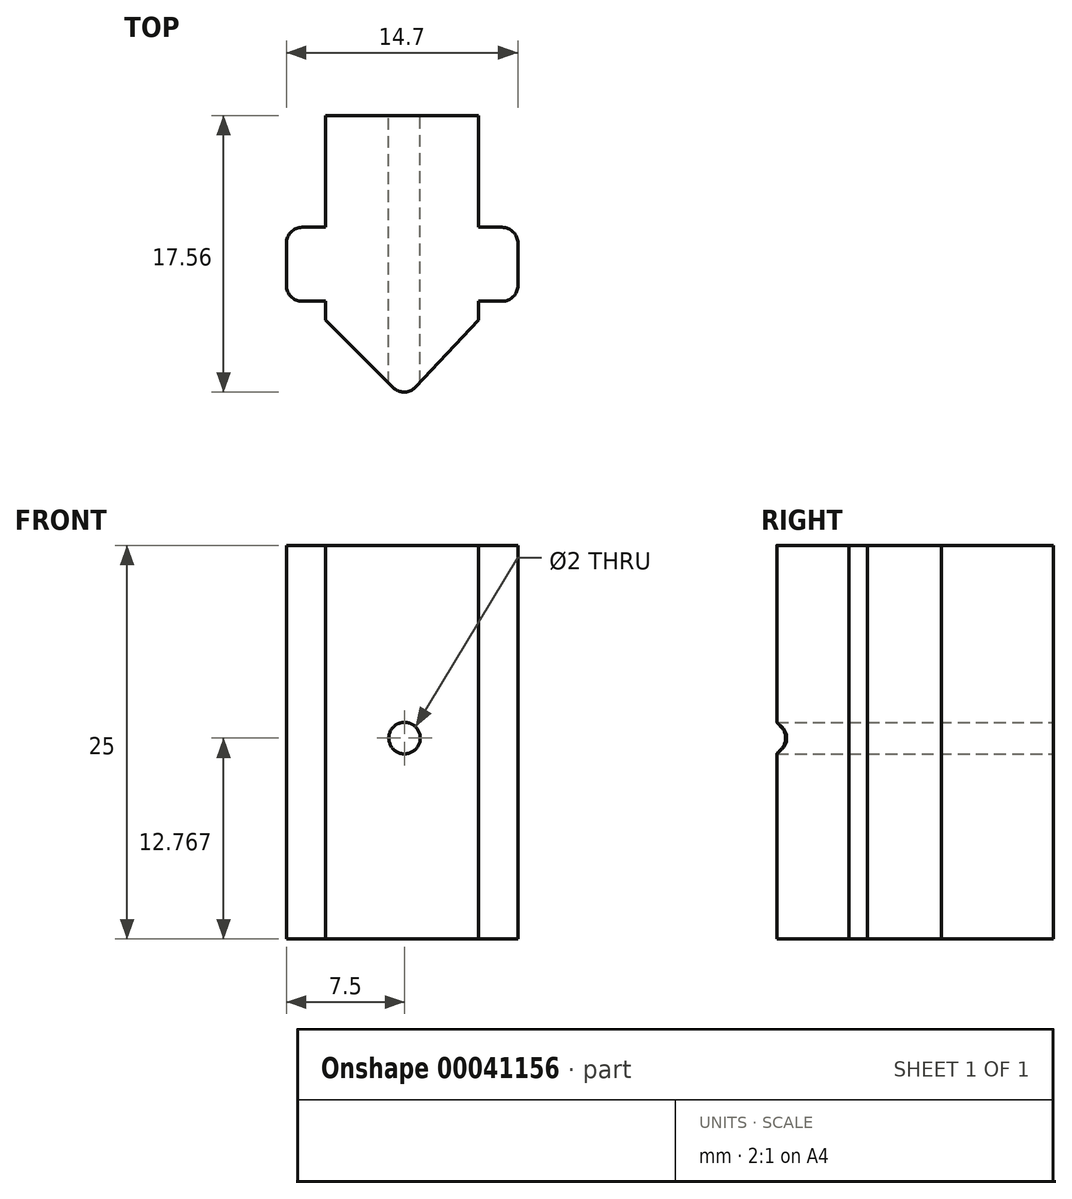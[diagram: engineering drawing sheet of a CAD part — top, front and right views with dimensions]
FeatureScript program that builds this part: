
annotation { "Feature Type Name" : "Feature", "Feature Type Description" : "" }
export const myFeature = defineFeature(function(context is Context, id is Id, definition is map)
    precondition{}
    {
        {
            var Q0;
            Q0=qCreatedBy(makeId("Top.planeOp"),FACE);
            var sketch = newSketch(context, id + "F0", { "sketchPlane" : qUnion([Q0])});
            skLineSegment(sketch, "E0.bottom", {"start": v(-5, 3.37) * mm, "end": v(4.7, 3.37) * mm});
            skLineSegment(sketch, "E0.top", {"start": v(-5, -9.63) * mm, "end": v(4.7, -9.63) * mm});
            skLineSegment(sketch, "E0.left", {"start": v(-5, 3.37) * mm, "end": v(-5, -9.63) * mm});
            skLineSegment(sketch, "E0.right", {"start": v(4.7, 3.37) * mm, "end": v(4.7, -9.63) * mm});
            skLineSegment(sketch, "E1.bottom", {"start": v(7.2, -3.73) * mm, "end": v(-7.5, -3.73) * mm});
            skLineSegment(sketch, "E1.top", {"start": v(7.2, -8.43) * mm, "end": v(-7.5, -8.43) * mm});
            skLineSegment(sketch, "E1.left", {"start": v(7.2, -3.73) * mm, "end": v(7.2, -8.43) * mm});
            skLineSegment(sketch, "E1.right", {"start": v(-7.5, -3.73) * mm, "end": v(-7.5, -8.43) * mm});
            skLineSegment(sketch, "E2", {"start": v(-5, -9.63) * mm, "end": v(0, -14.63) * mm});
            skLineSegment(sketch, "E3", {"start": v(0, -14.63) * mm, "end": v(4.7, -9.63) * mm});
            skSolve(sketch);
        }
        {
            var Q0;
            Q0=qSketchRegion(id+"F0",true);
            extrude(context, id + "F1", {"entities" : qUnion([Q0]), "depth" : 25 * mm});
        }
        {
            var Q0;
            Q0=makeQuery(id+"F1.opExtrude","SWEPT_EDGE",EDGE,{"disambiguationData":[OSD([sQuery(id+"F0.wireOp",EDGE,"E1.bottom"),sQuery(id+"F0.wireOp",EDGE,"E1.right")])]});
            var Q1;
            Q1=makeQuery(id+"F1.opExtrude","SWEPT_EDGE",EDGE,{"disambiguationData":[OSD([sQuery(id+"F0.wireOp",EDGE,"E1.top"),sQuery(id+"F0.wireOp",EDGE,"E1.right")])]});
            var Q2;
            Q2=makeQuery(id+"F1.opExtrude","SWEPT_EDGE",EDGE,{"disambiguationData":[OSD([sQuery(id+"F0.wireOp",EDGE,"E1.bottom"),sQuery(id+"F0.wireOp",EDGE,"E1.left")])]});
            var Q3;
            Q3=makeQuery(id+"F1.opExtrude","SWEPT_EDGE",EDGE,{"disambiguationData":[OSD([sQuery(id+"F0.wireOp",EDGE,"E1.top"),sQuery(id+"F0.wireOp",EDGE,"E1.left")])]});
            var Q4;
            Q4=makeQuery(id+"F1.opExtrude","SWEPT_EDGE",EDGE,{"disambiguationData":[OSD([sQuery(id+"F0.wireOp",EDGE,"E2"),sQuery(id+"F0.wireOp",EDGE,"E3")])]});
            fillet(context, id + "F2", {"entities" : qUnion([Q0, Q1, Q2, Q3, Q4]), "radius" : 1 * mm, "tangentPropagation" : true, "allowEdgeOverflow" : false});
        }
        {
            var Q0;
            Q0=makeQuery(id+"F1.opExtrude","SWEPT_FACE",FACE,{"disambiguationData":[OSD([sQuery(id+"F0.wireOp",EDGE,"E0.bottom")])]});
            var sketch = newSketch(context, id + "F3", { "sketchPlane" : qUnion([Q0])});
            skCircle(sketch, "E4", {"center": v(0, 12.77) * mm, "radius": 1 * mm});
            skSolve(sketch);
        }
        {
            var Q0;
            Q0 = qSketchRegion(id + "F3", true);
            extrude(context, id + "F4", {"entities" : qUnion([Q0]), "operationType" : NewBodyOperationType.REMOVE, "endBound" : BoundingType.THROUGH_ALL, "oppositeDirection" : true, "depth" : 25 * mm});
        }
        {
            var Q0;
            Q0=makeQuery(id+"F1.opExtrude","SWEPT_FACE",FACE,{"disambiguationData":[OSD([sQuery(id+"F0.wireOp",EDGE,"E0.bottom")])]});
            var sketch = newSketch(context, id + "F5", { "sketchPlane" : qUnion([Q0])});
            skCircle(sketch, "E5", {"center": v(0, 18.79) * mm, "radius": 1 * mm});
            skSolve(sketch);
        }
        {
            var Q0;
            Q0 = qSketchRegion(id + "F5", true);
            extrude(context, id + "F6", {"entities" : qUnion([Q0]), "operationType" : NewBodyOperationType.REMOVE, "depth" : 22.3 * mm});
        }
    });
